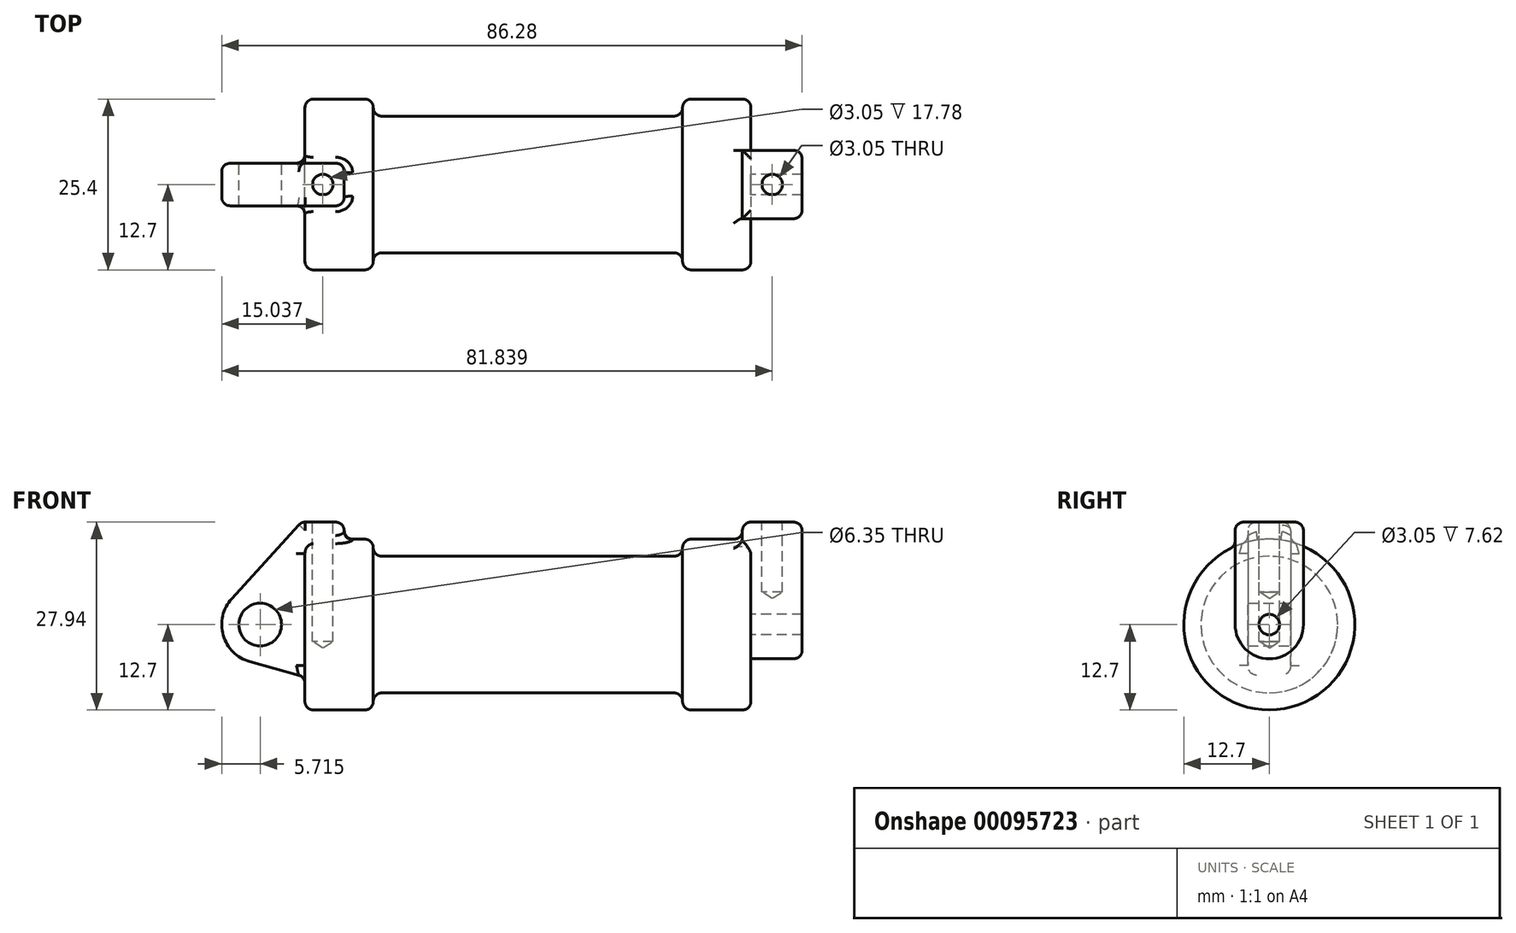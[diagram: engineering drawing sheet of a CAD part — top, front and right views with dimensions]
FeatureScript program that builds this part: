
annotation { "Feature Type Name" : "Feature", "Feature Type Description" : "" }
export const myFeature = defineFeature(function(context is Context, id is Id, definition is map)
    precondition{}
    {
        {
            var Q0;
            Q0=qCreatedBy(makeId("Front.planeOp"),FACE);
            var sketch = newSketch(context, id + "F0", { "sketchPlane" : qUnion([Q0])});
            skLineSegment(sketch, "E0", {"start": v(0, 0) * mm, "end": v(0, 12.7) * mm});
            skLineSegment(sketch, "E1", {"start": v(0, 12.7) * mm, "end": v(10.16, 12.7) * mm});
            skLineSegment(sketch, "E2", {"start": v(10.16, 12.7) * mm, "end": v(10.16, 10.16) * mm});
            skLineSegment(sketch, "E3", {"start": v(10.16, 10.16) * mm, "end": v(56.13, 10.16) * mm});
            skLineSegment(sketch, "E4", {"start": v(56.13, 10.16) * mm, "end": v(56.13, 12.7) * mm});
            skLineSegment(sketch, "E5", {"start": v(56.13, 12.7) * mm, "end": v(66.3, 12.7) * mm});
            skLineSegment(sketch, "E6", {"start": v(66.3, 12.7) * mm, "end": v(66.3, 0) * mm});
            skLineSegment(sketch, "E7", {"start": v(66.3, 0) * mm, "end": v(0, 0) * mm});
            skLineSegment(sketch, "E8", {"start": v(5.84, 15.24) * mm, "end": v(-0.5, 15.24) * mm});
            skLineSegment(sketch, "E9", {"start": v(-0.5, 15.24) * mm, "end": v(-10.88, 3.85) * mm});
            skLineSegment(sketch, "E10", {"start": v(0, 0) * mm, "end": v(-6.65, 0) * mm});
            skCircle(sketch, "E11", {"center": v(-6.65, 0) * mm, "radius": 5.72 * mm});
            skCircle(sketch, "E12", {"center": v(-6.65, 0) * mm, "radius": 3.18 * mm});
            skLineSegment(sketch, "E13", {"start": v(5.84, 15.24) * mm, "end": v(5.84, -9.4) * mm});
            skLineSegment(sketch, "E14", {"start": v(5.84, -9.4) * mm, "end": v(-8.18, -5.5) * mm});
            skSolve(sketch);
        }
        {
            var Q0;
            {var subQ0=sQuery(id+"F0.wireOp",EDGE,"E2");Q0=makeQuery(id+"F0.imprint","IMPRINT",FACE,{"disambiguationData":[TD([[makeQuery(id+"F0.imprint","IMPRINT",EDGE,{"derivedFrom":subQ0}),-1.0]])]});}
            var Q1;
            {var subQ0=sQuery(id+"F0.wireOp",EDGE,"E0");Q1=makeQuery(id+"F0.imprint","IMPRINT",FACE,{"disambiguationData":[TD([[makeQuery(id+"F0.imprint","IMPRINT",EDGE,{"derivedFrom":subQ0}),-1.0]])]});}
            var Q2;
            Q2=sQuery(id+"F0.wireOp",EDGE,"E7");
            revolve(context, id + "F1", {"entities" : qUnion([Q0, Q1]), "axis" : qUnion([Q2]), "revolveType" : RevolveType.FULL});
        }
        {
            var Q0;
            {var subQ4=sQuery(id+"F0.wireOp",EDGE,"E12");Q0=makeQuery(id+"F0.imprint","IMPRINT",FACE,{"disambiguationData":[TD([[makeQuery(id+"F0.imprint","IMPRINT",EDGE,{"derivedFrom":subQ4}),-1.0]])]});}
            var Q1;
            {var subQ3=sQuery(id+"F0.wireOp",EDGE,"E0");Q1=makeQuery(id+"F0.imprint","IMPRINT",FACE,{"disambiguationData":[TD([[makeQuery(id+"F0.imprint","IMPRINT",EDGE,{"derivedFrom":subQ3}),1.0]])]});}
            var Q2;
            {var subQ0=sQuery(id+"F0.wireOp",EDGE,"E0");Q2=makeQuery(id+"F0.imprint","IMPRINT",FACE,{"disambiguationData":[TD([[makeQuery(id+"F0.imprint","IMPRINT",EDGE,{"derivedFrom":subQ0}),-1.0]])]});}
            var Q3;
            {var subQ0=sQuery(id+"F0.wireOp",EDGE,"E14");Q3=makeQuery(id+"F0.imprint","IMPRINT",FACE,{"disambiguationData":[TD([[makeQuery(id+"F0.imprint","IMPRINT",EDGE,{"derivedFrom":subQ0}),-1.0]])]});}
            extrude(context, id + "F2", {"entities" : qUnion([Q0, Q1, Q2, Q3]), "operationType" : NewBodyOperationType.ADD, "endBound" : BoundingType.SYMMETRIC, "depth" : 6.35 * mm});
        }
        {
            var Q0;
            Q0=makeQuery(id+"F1.opRevolve","SWEPT_FACE",FACE,{"disambiguationData":[OSD([sQuery(id+"F0.wireOp",EDGE,"E6")])]});
            var sketch = newSketch(context, id + "F3", { "sketchPlane" : qUnion([Q0])});
            skCircle(sketch, "E15", {"center": v(0, 0) * mm, "radius": 1.52 * mm});
            skCircle(sketch, "E16", {"center": v(0, 0) * mm, "radius": 5.08 * mm});
            skLineSegment(sketch, "E17", {"start": v(-5.08, 0) * mm, "end": v(-5.08, 15.24) * mm});
            skLineSegment(sketch, "E18", {"start": v(-5.08, 15.24) * mm, "end": v(5.08, 15.24) * mm});
            skLineSegment(sketch, "E19", {"start": v(5.08, 15.24) * mm, "end": v(5.08, 0) * mm});
            skSolve(sketch);
        }
        {
            var Q0;
            {var subQ0=sQuery(id+"F3.wireOp",EDGE,"E17");var subQ1=sQuery(id+"F3.wireOp",EDGE,"E16");var subQ2=makeQuery(id+"F3.imprint","INTERSECT",VERTEX,{"derivedFrom":[subQ1,subQ0]});Q0=makeQuery(id+"F3.imprint","IMPRINT",FACE,{"disambiguationData":[TD([[makeQuery(id+"F3.imprint","IMPRINT",EDGE,{"disambiguationData":[TD([[subQ2,1.0]])],"derivedFrom":subQ1}),-1.0]])]});}
            var Q1;
            {var subQ0=sQuery(id+"F3.wireOp",EDGE,"E18");Q1=makeQuery(id+"F3.imprint","IMPRINT",FACE,{"disambiguationData":[TD([[makeQuery(id+"F3.imprint","IMPRINT",EDGE,{"derivedFrom":subQ0}),-1.0]])]});}
            var Q2;
            Q2=makeQuery(id+"F3.imprint","IMPRINT",FACE,{"disambiguationData":[TD([[makeQuery(id+"F3.imprint","IMPRINT",EDGE,{"derivedFrom":sQuery(id+"F3.wireOp",EDGE,"E15")}),-1.0]])]});
            extrude(context, id + "F4", {"entities" : qUnion([Q0, Q1, Q2]), "operationType" : NewBodyOperationType.ADD, "depth" : 7.62 * mm, "hasSecondDirection" : true, "secondDirectionOppositeDirection" : true, "secondDirectionDepth" : 1.27 * mm});
        }
        {
            var Q0;
            Q0=makeQuery(id+"F4.opExtrude","SWEPT_FACE",FACE,{"disambiguationData":[OSD([sQuery(id+"F3.wireOp",EDGE,"E18")])]});
            var sketch = newSketch(context, id + "F5", { "sketchPlane" : qUnion([Q0])});
            skPoint(sketch, "E20", {"position": v(69.47, 0) * mm});
            skPoint(sketch, "E21", {"position": v(2.67, 0) * mm});
            skLineSegment(sketch, "E22", {"start": v(65.02, 0) * mm, "end": v(73.91, 0) * mm, "construction": true});
            skSolve(sketch);
        }
        {
            var Q0;
            Q0=sQuery(id+"F5.wireOp",VERTEX,"E21");
            var Q1;
            Q1=makeQuery(id+"F1.opRevolve","SWEPT_BODY",BODY,{"disambiguationData":[OSD([sQuery(id+"F0.wireOp",EDGE,"E0"),sQuery(id+"F0.wireOp",EDGE,"E1"),sQuery(id+"F0.wireOp",EDGE,"E2"),sQuery(id+"F0.wireOp",EDGE,"E3"),sQuery(id+"F0.wireOp",EDGE,"E4"),sQuery(id+"F0.wireOp",EDGE,"E5"),sQuery(id+"F0.wireOp",EDGE,"E6"),sQuery(id+"F0.wireOp",EDGE,"E7")])]});
            hole(context, id + "F6", {"style" : HoleStyle.SIMPLE, "endStyle" : HoleEndStyle.BLIND, "holeDiameter" : 3.05 * mm, "holeDepth" : 17.78 * mm, "startFromSketch" : true, "locations" : qUnion([Q0]), "scope" : qUnion([Q1])});
        }
        {
            var Q0;
            Q0=sQuery(id+"F5.wireOp",VERTEX,"E20");
            var Q1;
            Q1=makeQuery(id+"F1.opRevolve","SWEPT_BODY",BODY,{"disambiguationData":[OSD([sQuery(id+"F0.wireOp",EDGE,"E0"),sQuery(id+"F0.wireOp",EDGE,"E1"),sQuery(id+"F0.wireOp",EDGE,"E2"),sQuery(id+"F0.wireOp",EDGE,"E3"),sQuery(id+"F0.wireOp",EDGE,"E4"),sQuery(id+"F0.wireOp",EDGE,"E5"),sQuery(id+"F0.wireOp",EDGE,"E6"),sQuery(id+"F0.wireOp",EDGE,"E7")])]});
            hole(context, id + "F7", {"style" : HoleStyle.SIMPLE, "endStyle" : HoleEndStyle.BLIND, "holeDiameter" : 3.05 * mm, "holeDepth" : 10.4 * mm, "startFromSketch" : true, "locations" : qUnion([Q0]), "scope" : qUnion([Q1])});
        }
        {
            var Q0;
            Q0=makeQuery(id+"F1.opRevolve","SWEPT_EDGE",EDGE,{"disambiguationData":[OSD([sQuery(id+"F0.wireOp",EDGE,"E2"),sQuery(id+"F0.wireOp",EDGE,"E3")])]});
            fillet(context, id + "F8", {"entities" : qUnion([Q0]), "radius" : 1.27 * mm, "tangentPropagation" : true, "allowEdgeOverflow" : false});
        }
        {
            var Q0;
            Q0=makeQuery(id+"F1.opRevolve","SWEPT_EDGE",EDGE,{"disambiguationData":[OSD([sQuery(id+"F0.wireOp",EDGE,"E1"),sQuery(id+"F0.wireOp",EDGE,"E2")])]});
            fillet(context, id + "F9", {"entities" : qUnion([Q0]), "radius" : 1.27 * mm, "tangentPropagation" : true, "allowEdgeOverflow" : false});
        }
        {
            var Q0;
            Q0=makeQuery(id+"F2.opExtrude","CAP_EDGE",EDGE,{"disambiguationData":[OSD([sQuery(id+"F0.wireOp",EDGE,"E13")])],"isStart":false});
            fillet(context, id + "F10", {"entities" : qUnion([Q0]), "radius" : 1.27 * mm, "tangentPropagation" : true, "allowEdgeOverflow" : false});
        }
        {
            var Q0;
            Q0=makeQuery(id+"F2.opExtrude","CAP_EDGE",EDGE,{"disambiguationData":[OSD([sQuery(id+"F0.wireOp",EDGE,"E13")])],"isStart":true});
            var Q1;
            Q1=makeQuery(id+"F2.opExtrude","SWEPT_FACE",FACE,{"disambiguationData":[OSD([sQuery(id+"F0.wireOp",EDGE,"E13")])]});
            fillet(context, id + "F11", {"entities" : qUnion([Q0, Q1]), "radius" : 1.27 * mm, "tangentPropagation" : true, "allowEdgeOverflow" : false});
        }
        {
            var Q0;
            Q0=makeQuery(id+"F2.opExtrude","SWEPT_FACE",FACE,{"disambiguationData":[OSD([sQuery(id+"F0.wireOp",EDGE,"E9")])]});
            fillet(context, id + "F12", {"entities" : qUnion([Q0]), "radius" : 1.27 * mm, "tangentPropagation" : true, "allowEdgeOverflow" : false});
        }
        {
            var Q0;
            Q0=makeQuery(id+"F2.opExtrude","CAP_EDGE",EDGE,{"disambiguationData":[OSD([sQuery(id+"F0.wireOp",EDGE,"E8")])],"isStart":true});
            fillet(context, id + "F13", {"entities" : qUnion([Q0]), "radius" : 1.27 * mm, "tangentPropagation" : true, "allowEdgeOverflow" : false});
        }
        {
            var Q0;
            Q0=makeQuery(id+"F1.opRevolve","SWEPT_EDGE",EDGE,{"disambiguationData":[OSD([sQuery(id+"F0.wireOp",EDGE,"E0"),sQuery(id+"F0.wireOp",EDGE,"E1")])]});
            fillet(context, id + "F14", {"entities" : qUnion([Q0]), "radius" : 1.27 * mm, "tangentPropagation" : true, "allowEdgeOverflow" : false});
        }
        {
            var Q0;
            Q0=makeQuery(id+"F2.boolean.opBoolean","INTERSECT",EDGE,{"derivedFrom":[makeQuery(id+"F1.opRevolve","SWEPT_FACE",FACE,{"disambiguationData":[OSD([sQuery(id+"F0.wireOp",EDGE,"E0")])]}),makeQuery(id+"F2.opExtrude","CAP_FACE",FACE,{"disambiguationData":[OSD([sQuery(id+"F0.wireOp",EDGE,"E8"),sQuery(id+"F0.wireOp",EDGE,"E9"),sQuery(id+"F0.wireOp",EDGE,"E11"),sQuery(id+"F0.wireOp",EDGE,"E12"),sQuery(id+"F0.wireOp",EDGE,"E13"),sQuery(id+"F0.wireOp",EDGE,"E14")])],"isStart":false})]});
            var Q1;
            Q1=makeQuery(id+"F12.opFillet","BLEND_EDGE",EDGE,{"blendedFrom":[makeQuery(id+"F2.opExtrude","CAP_EDGE",EDGE,{"disambiguationData":[OSD([sQuery(id+"F0.wireOp",EDGE,"E14")])],"isStart":false}),makeQuery(id+"F1.opRevolve","SWEPT_FACE",FACE,{"disambiguationData":[OSD([sQuery(id+"F0.wireOp",EDGE,"E0")])]})],"blendedInto":[makeQuery(id+"F1.opRevolve","SWEPT_FACE",FACE,{"disambiguationData":[OSD([sQuery(id+"F0.wireOp",EDGE,"E0")])]})]});
            var Q2;
            Q2=makeQuery(id+"F2.boolean.opBoolean","INTERSECT",EDGE,{"derivedFrom":[makeQuery(id+"F1.opRevolve","SWEPT_FACE",FACE,{"disambiguationData":[OSD([sQuery(id+"F0.wireOp",EDGE,"E0")])]}),makeQuery(id+"F2.opExtrude","SWEPT_FACE",FACE,{"disambiguationData":[OSD([sQuery(id+"F0.wireOp",EDGE,"E14")])]})]});
            var Q3;
            Q3=makeQuery(id+"F12.opFillet","BLEND_EDGE",EDGE,{"blendedFrom":[makeQuery(id+"F2.opExtrude","CAP_EDGE",EDGE,{"disambiguationData":[OSD([sQuery(id+"F0.wireOp",EDGE,"E14")])],"isStart":true}),makeQuery(id+"F1.opRevolve","SWEPT_FACE",FACE,{"disambiguationData":[OSD([sQuery(id+"F0.wireOp",EDGE,"E0")])]})],"blendedInto":[makeQuery(id+"F1.opRevolve","SWEPT_FACE",FACE,{"disambiguationData":[OSD([sQuery(id+"F0.wireOp",EDGE,"E0")])]})]});
            var Q4;
            Q4=makeQuery(id+"F2.boolean.opBoolean","INTERSECT",EDGE,{"derivedFrom":[makeQuery(id+"F1.opRevolve","SWEPT_FACE",FACE,{"disambiguationData":[OSD([sQuery(id+"F0.wireOp",EDGE,"E0")])]}),makeQuery(id+"F2.opExtrude","CAP_FACE",FACE,{"disambiguationData":[OSD([sQuery(id+"F0.wireOp",EDGE,"E8"),sQuery(id+"F0.wireOp",EDGE,"E9"),sQuery(id+"F0.wireOp",EDGE,"E11"),sQuery(id+"F0.wireOp",EDGE,"E12"),sQuery(id+"F0.wireOp",EDGE,"E13"),sQuery(id+"F0.wireOp",EDGE,"E14")])],"isStart":true})]});
            fillet(context, id + "F15", {"entities" : qUnion([Q0, Q1, Q2, Q3, Q4]), "radius" : 1.27 * mm, "tangentPropagation" : true, "allowEdgeOverflow" : false});
        }
        {
            var Q0;
            Q0=makeQuery(id+"F1.opRevolve","SWEPT_EDGE",EDGE,{"disambiguationData":[OSD([sQuery(id+"F0.wireOp",EDGE,"E3"),sQuery(id+"F0.wireOp",EDGE,"E4")])]});
            var Q1;
            Q1=makeQuery(id+"F1.opRevolve","SWEPT_EDGE",EDGE,{"disambiguationData":[OSD([sQuery(id+"F0.wireOp",EDGE,"E4"),sQuery(id+"F0.wireOp",EDGE,"E5")])]});
            fillet(context, id + "F16", {"entities" : qUnion([Q0, Q1]), "radius" : 1.27 * mm, "tangentPropagation" : true, "allowEdgeOverflow" : false});
        }
        {
            var Q0;
            Q0=makeQuery(id+"F4.boolean.opBoolean","INTERSECT",EDGE,{"derivedFrom":[makeQuery(id+"F1.opRevolve","SWEPT_FACE",FACE,{"disambiguationData":[OSD([sQuery(id+"F0.wireOp",EDGE,"E5")])]}),makeQuery(id+"F4.opExtrude","CAP_FACE",FACE,{"disambiguationData":[OSD([sQuery(id+"F3.wireOp",EDGE,"E15"),sQuery(id+"F3.wireOp",EDGE,"E16"),sQuery(id+"F3.wireOp",EDGE,"E17"),sQuery(id+"F3.wireOp",EDGE,"E18"),sQuery(id+"F3.wireOp",EDGE,"E19")])],"isStart":true})]});
            var Q1;
            Q1=makeQuery(id+"F4.boolean.opBoolean","INTERSECT",EDGE,{"derivedFrom":[makeQuery(id+"F1.opRevolve","SWEPT_FACE",FACE,{"disambiguationData":[OSD([sQuery(id+"F0.wireOp",EDGE,"E5")])]}),makeQuery(id+"F4.opExtrude","SWEPT_FACE",FACE,{"disambiguationData":[OSD([sQuery(id+"F3.wireOp",EDGE,"E17")])]})]});
            fillet(context, id + "F17", {"entities" : qUnion([Q0, Q1]), "radius" : 1.27 * mm, "tangentPropagation" : true, "allowEdgeOverflow" : false});
        }
        {
            var Q0;
            Q0=makeQuery(id+"F1.opRevolve","SWEPT_EDGE",EDGE,{"disambiguationData":[OSD([sQuery(id+"F0.wireOp",EDGE,"E5"),sQuery(id+"F0.wireOp",EDGE,"E6")])]});
            fillet(context, id + "F18", {"entities" : qUnion([Q0]), "radius" : 1.27 * mm, "tangentPropagation" : true, "allowEdgeOverflow" : false});
        }
        {
            var Q0;
            Q0=makeQuery(id+"F4.opExtrude","CAP_EDGE",EDGE,{"disambiguationData":[OSD([sQuery(id+"F3.wireOp",EDGE,"E16")])],"isStart":false});
            var Q1;
            Q1=makeQuery(id+"F4.opExtrude","CAP_EDGE",EDGE,{"disambiguationData":[OSD([sQuery(id+"F3.wireOp",EDGE,"E19")])],"isStart":false});
            fillet(context, id + "F19", {"entities" : qUnion([Q0, Q1]), "radius" : 1.27 * mm, "tangentPropagation" : true, "allowEdgeOverflow" : false});
        }
        {
            var Q0;
            Q0=makeQuery(id+"F4.opExtrude","SWEPT_EDGE",EDGE,{"disambiguationData":[OSD([sQuery(id+"F3.wireOp",EDGE,"E18"),sQuery(id+"F3.wireOp",EDGE,"E19")])]});
            var Q1;
            Q1=makeQuery(id+"F4.opExtrude","SWEPT_EDGE",EDGE,{"disambiguationData":[OSD([sQuery(id+"F3.wireOp",EDGE,"E17"),sQuery(id+"F3.wireOp",EDGE,"E18")])]});
            var Q2;
            Q2=makeQuery(id+"F4.opExtrude","CAP_EDGE",EDGE,{"disambiguationData":[OSD([sQuery(id+"F3.wireOp",EDGE,"E18")])],"isStart":true});
            fillet(context, id + "F20", {"entities" : qUnion([Q0, Q1, Q2]), "radius" : 1.27 * mm, "tangentPropagation" : true, "allowEdgeOverflow" : false});
        }
    });
